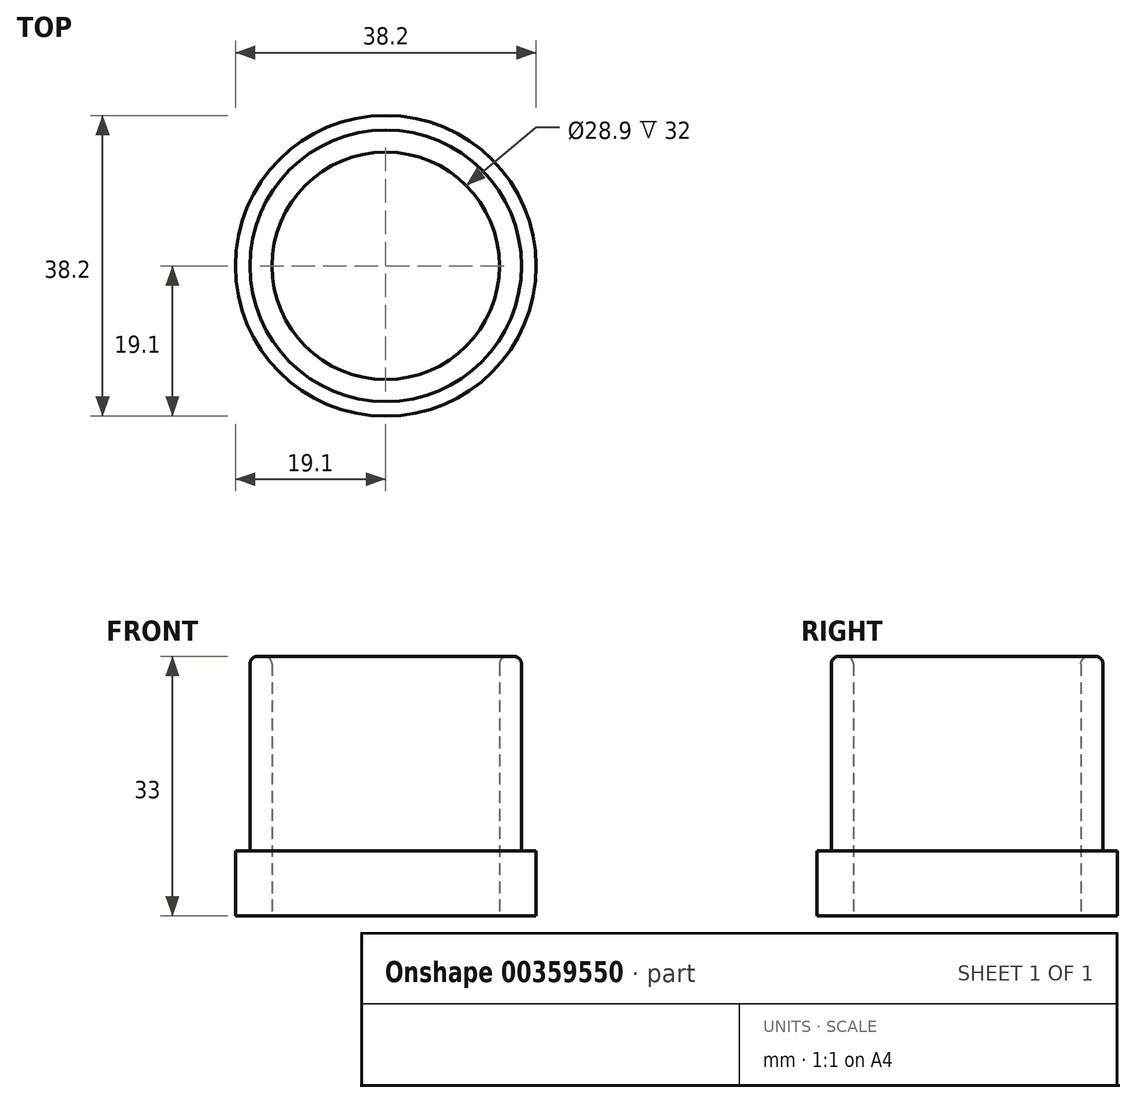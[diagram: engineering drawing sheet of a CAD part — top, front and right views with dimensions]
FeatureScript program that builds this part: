
annotation { "Feature Type Name" : "Feature", "Feature Type Description" : "" }
export const myFeature = defineFeature(function(context is Context, id is Id, definition is map)
    precondition{}
    {
        {
            var Q0;
            Q0=qCreatedBy(makeId("Top.planeOp"),FACE);
            var sketch = newSketch(context, id + "F0", { "sketchPlane" : qUnion([Q0])});
            skCircle(sketch, "E0", {"center": v(0, 0) * mm, "radius": 19.1 * mm});
            skCircle(sketch, "E1", {"center": v(0, 0) * mm, "radius": 17.25 * mm});
            skCircle(sketch, "E2", {"center": v(0, 0) * mm, "radius": 14.45 * mm});
            skSolve(sketch);
        }
        {
            var Q0;
            Q0=makeQuery(id+"F0.imprint","IMPRINT",FACE,{"disambiguationData":[TD([[makeQuery(id+"F0.imprint","IMPRINT",EDGE,{"derivedFrom":sQuery(id+"F0.wireOp",EDGE,"E1")}),1.0]])]});
            extrude(context, id + "F1", {"entities" : qUnion([Q0]), "depth" : 33 * mm});
        }
        {
            var Q0;
            Q0 = qSketchRegion(id + "F0", true);
            extrude(context, id + "F2", {"entities" : qUnion([Q0]), "operationType" : NewBodyOperationType.ADD, "depth" : 8.3 * mm});
        }
        {
            var Q0;
            Q0=makeQuery(id+"F1.opExtrude","CAP_EDGE",EDGE,{"disambiguationData":[OSD([sQuery(id+"F0.wireOp",EDGE,"E1")])],"isStart":false});
            var Q1;
            Q1=makeQuery(id+"F1.opExtrude","CAP_EDGE",EDGE,{"disambiguationData":[OSD([sQuery(id+"F0.wireOp",EDGE,"E2")])],"isStart":false});
            fillet(context, id + "F3", {"entities" : qUnion([Q0, Q1]), "radius" : 1 * mm, "tangentPropagation" : true, "allowEdgeOverflow" : false});
        }
    });
